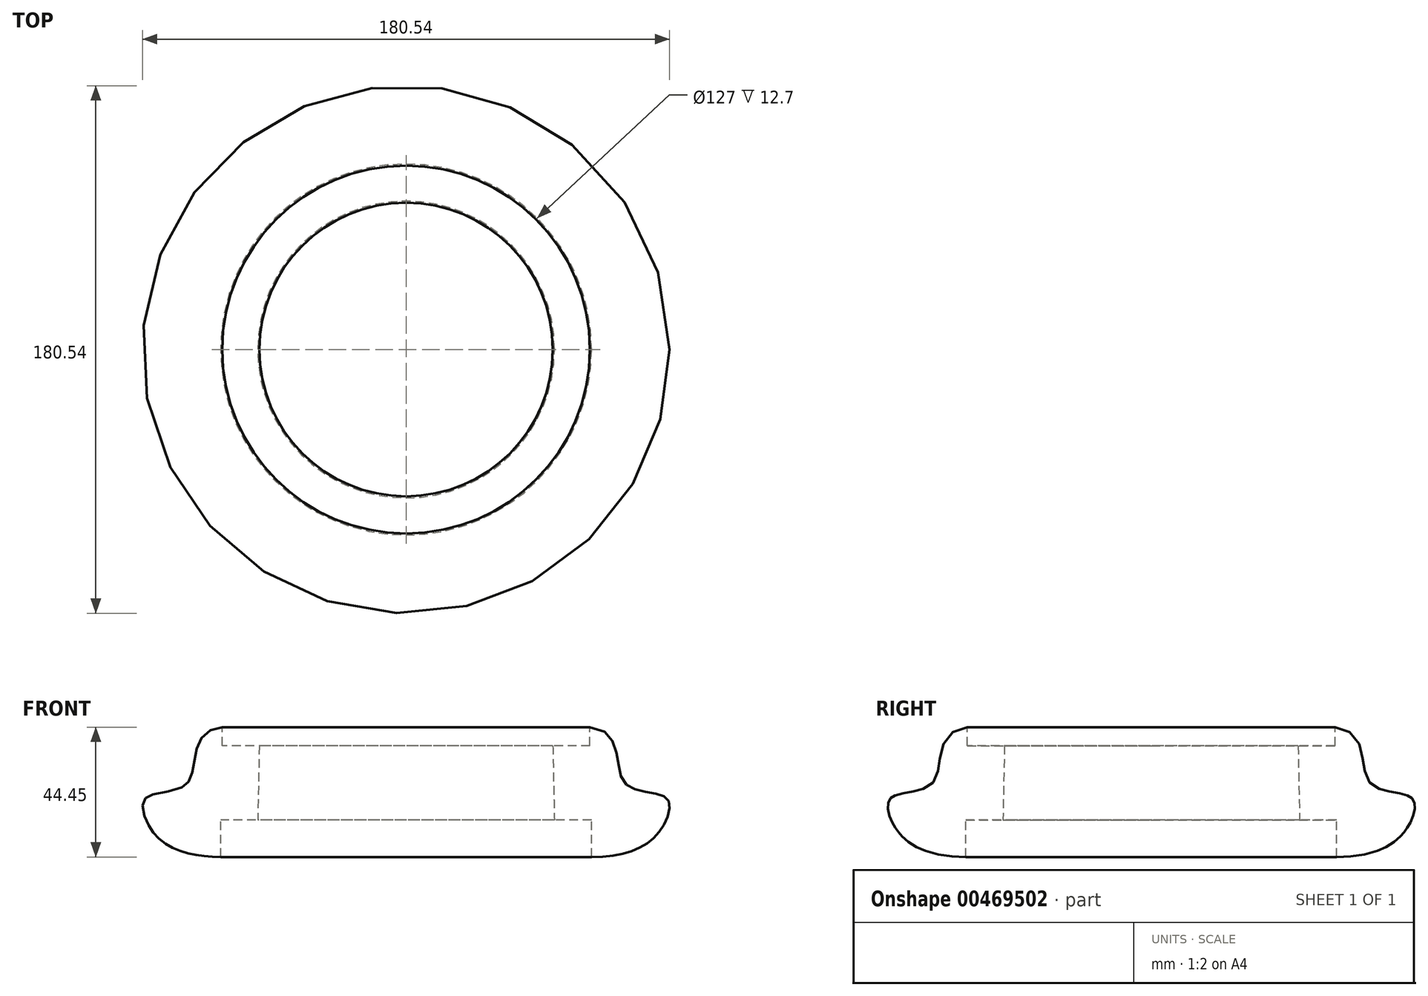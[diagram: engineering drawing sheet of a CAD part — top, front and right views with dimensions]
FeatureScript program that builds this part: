
annotation { "Feature Type Name" : "Feature", "Feature Type Description" : "" }
export const myFeature = defineFeature(function(context is Context, id is Id, definition is map)
    precondition{}
    {
        {
            var Q0;
            Q0=qCreatedBy(makeId("Front.planeOp"),FACE);
            var sketch = newSketch(context, id + "F0", { "sketchPlane" : qUnion([Q0])});
            skLineSegment(sketch, "E0", {"start": v(0, 0) * mm, "end": v(-63.5, 0) * mm, "construction": true});
            skLineSegment(sketch, "E1", {"start": v(-63.5, 0) * mm, "end": v(-63.5, 38.1) * mm, "construction": true});
            skSolve(sketch);
        }
        {
            var Q0;
            Q0=qCreatedBy(makeId("Front.planeOp"),FACE);
            var sketch = newSketch(context, id + "F1", { "sketchPlane" : qUnion([Q0])});
            skLineSegment(sketch, "E2", {"start": v(-50.8, 12.7) * mm, "end": v(-63.5, 12.7) * mm});
            skLineSegment(sketch, "E3", {"start": v(-63.5, 12.7) * mm, "end": v(-63.5, 0) * mm});
            skLineSegment(sketch, "E4", {"start": v(-50.27, 38.1) * mm, "end": v(-62.97, 38.1) * mm});
            skLineSegment(sketch, "E5", {"start": v(-62.97, 38.1) * mm, "end": v(-62.97, 44.45) * mm});
            skFitSpline(sketch, "E6", {"points": [v(-62.97, 44.45) * mm, v(-74.65, 25.59) * mm, v(-89.06, 20.3) * mm, v(-88.25, 10.96) * mm, v(-79.73, 3.05) * mm, v(-63.5, 0) * mm], "startDerivative": vector(-145.8, -15.4) * mm, "endDerivative": vector(90.05, 0) * mm});
            skLineSegment(sketch, "E7", {"start": v(-50.27, 38.1) * mm, "end": v(-50.8, 12.7) * mm});
            skLineSegment(sketch, "E8", {"start": v(0, 38.42) * mm, "end": v(0, 0) * mm, "construction": true});
            skSolve(sketch);
        }
        {
            var Q0;
            Q0=makeQuery(id+"F1.imprint","IMPRINT",FACE,{"disambiguationData":[TD([[makeQuery(id+"F1.imprint","IMPRINT",EDGE,{"derivedFrom":sQuery(id+"F1.wireOp",EDGE,"E2")}),-1.0]])]});
            var Q1;
            Q1=sQuery(id+"F1.wireOp",EDGE,"E8");
            revolve(context, id + "F2", {"entities" : qUnion([Q0]), "axis" : qUnion([Q1]), "revolveType" : RevolveType.FULL});
        }
    });
